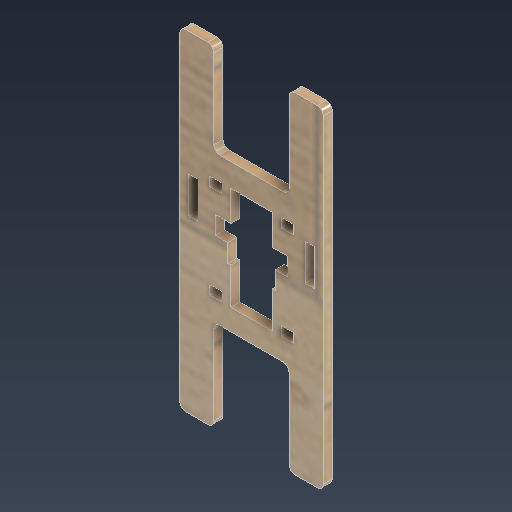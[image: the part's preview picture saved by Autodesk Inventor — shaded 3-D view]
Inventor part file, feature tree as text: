
AUTODESK INVENTOR PART (.ipt)
format: ipt  version: 2025.3 (Build 293356000, 356)  size: 278,016 bytes
history: native  units: mm
features: sketch x3, extrude x2, other x1
ambient origin geometry x8: Origin, YZ Plane, XZ Plane, XY Plane, X Axis, Y Axis, Z Axis, Center Point
bodies: Body1 (feature_tree)
feature tree (6):
  other  "實體1"
  extrude  "擠出1"  Depth=47.7mm
  sketch  "草圖3"
  extrude  "擠出4"  Depth=4.0mm
  sketch  "草圖1"
  sketch  "草圖5"
